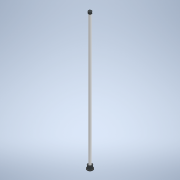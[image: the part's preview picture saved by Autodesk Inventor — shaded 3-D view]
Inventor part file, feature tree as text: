
AUTODESK INVENTOR PART (.ipt)
format: ipt  version: 2022 (Build 260153000, 153)  size: 109,568 bytes
history: native  units: in
note: dims shown in document units (in); Inventor stores cm internally (conversion verified against a paired STEP export)
features: extrude x4, sketch x4
ambient origin geometry x8: Origin, YZ Plane, XZ Plane, XY Plane, X Axis, Y Axis, Z Axis, Center Point
bodies: Solid1 (feature_tree)
feature tree (8):
  extrude  "Extrusion1"  Depth=41.3386in TaperAngle=0.0deg
  extrude  "Extrusion2"  Depth=0.9843in TaperAngle=0.0deg
  extrude  "Extrusion3"  Depth=0.1969in TaperAngle=0.0deg
  extrude  "Extrusion4"  Depth=0.5906in TaperAngle=0.0deg
  sketch  "Sketch1"  dims[d0=0.7874in d1=41.3386in d2=0.0in]
  sketch  "Sketch2"  dims[d3=1.378in d4=0.9843in d5=0.0in]
  sketch  "Sketch3"  dims[d6=1.7717in d7=0.1969in d8=0.0in]
  sketch  "Sketch4"  dims[d9=0.9843in d10=0.5906in d11=0.0in]
